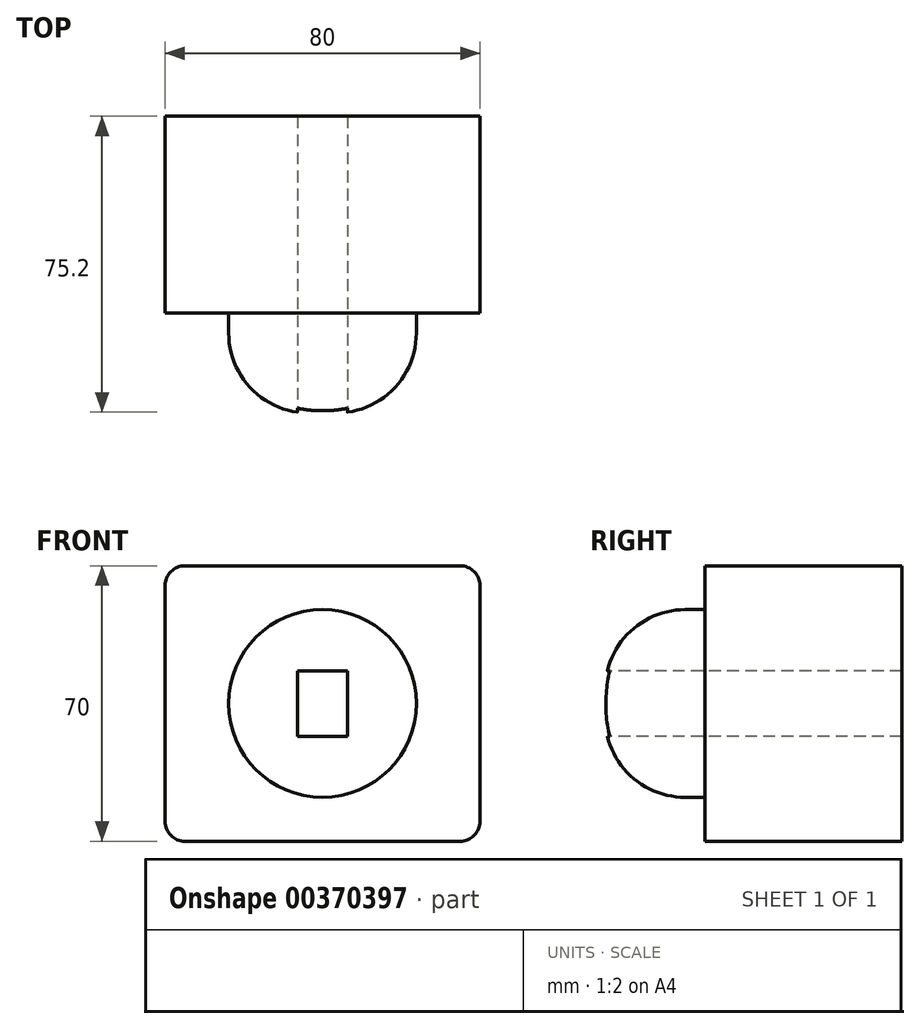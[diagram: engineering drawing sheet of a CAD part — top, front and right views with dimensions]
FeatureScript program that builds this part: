
annotation { "Feature Type Name" : "Feature", "Feature Type Description" : "" }
export const myFeature = defineFeature(function(context is Context, id is Id, definition is map)
    precondition{}
    {
        {
            var Q0;
            Q0=qCreatedBy(makeId("Front.planeOp"),FACE);
            var sketch = newSketch(context, id + "F0", { "sketchPlane" : qUnion([Q0])});
            skLineSegment(sketch, "E0.bottom", {"start": v(40, -35) * mm, "end": v(-40, -35) * mm});
            skLineSegment(sketch, "E0.top", {"start": v(40, 35) * mm, "end": v(-40, 35) * mm});
            skLineSegment(sketch, "E0.left", {"start": v(40, -35) * mm, "end": v(40, 35) * mm});
            skLineSegment(sketch, "E0.right", {"start": v(-40, -35) * mm, "end": v(-40, 35) * mm});
            skPoint(sketch, "E0.middle", {"position": v(0, 0) * mm});
            skSolve(sketch);
        }
        {
            var Q0;
            Q0=makeQuery(id+"F0.imprint","IMPRINT",FACE,{"disambiguationData":[TD([[makeQuery(id+"F0.imprint","IMPRINT",EDGE,{"derivedFrom":sQuery(id+"F0.wireOp",EDGE,"E0.bottom")}),-1.0]])]});
            extrude(context, id + "F1", {"entities" : qUnion([Q0]), "depth" : 50 * mm});
        }
        {
            var Q0;
            Q0=makeQuery(id+"F1.opExtrude","CAP_FACE",FACE,{"disambiguationData":[OSD([sQuery(id+"F0.wireOp",EDGE,"E0.bottom"),sQuery(id+"F0.wireOp",EDGE,"E0.top"),sQuery(id+"F0.wireOp",EDGE,"E0.left"),sQuery(id+"F0.wireOp",EDGE,"E0.right")])],"isStart":false});
            var sketch = newSketch(context, id + "F2", { "sketchPlane" : qUnion([Q0])});
            skCircle(sketch, "E1", {"center": v(0, 0) * mm, "radius": 23.84 * mm});
            skSolve(sketch);
        }
        {
            var Q0;
            Q0=makeQuery(id+"F2.imprint","IMPRINT",FACE,{"disambiguationData":[TD([[makeQuery(id+"F2.imprint","IMPRINT",EDGE,{"derivedFrom":sQuery(id+"F2.wireOp",EDGE,"E1")}),1.0]])]});
            extrude(context, id + "F3", {"entities" : qUnion([Q0]), "operationType" : NewBodyOperationType.ADD, "depth" : 25.4 * mm});
        }
        {
            var Q0;
            Q0=makeQuery(id+"F1.opExtrude","SWEPT_EDGE",EDGE,{"disambiguationData":[OSD([sQuery(id+"F0.wireOp",EDGE,"E0.top"),sQuery(id+"F0.wireOp",EDGE,"E0.left")])]});
            var Q1;
            Q1=makeQuery(id+"F1.opExtrude","SWEPT_EDGE",EDGE,{"disambiguationData":[OSD([sQuery(id+"F0.wireOp",EDGE,"E0.bottom"),sQuery(id+"F0.wireOp",EDGE,"E0.left")])]});
            var Q2;
            Q2=makeQuery(id+"F1.opExtrude","SWEPT_EDGE",EDGE,{"disambiguationData":[OSD([sQuery(id+"F0.wireOp",EDGE,"E0.top"),sQuery(id+"F0.wireOp",EDGE,"E0.right")])]});
            var Q3;
            Q3=makeQuery(id+"F1.opExtrude","SWEPT_EDGE",EDGE,{"disambiguationData":[OSD([sQuery(id+"F0.wireOp",EDGE,"E0.bottom"),sQuery(id+"F0.wireOp",EDGE,"E0.right")])]});
            fillet(context, id + "F4", {"entities" : qUnion([Q0, Q1, Q2, Q3]), "radius" : 5.08 * mm, "tangentPropagation" : true, "allowEdgeOverflow" : false});
        }
        {
            var Q0;
            Q0=makeQuery(id+"F3.opExtrude","CAP_EDGE",EDGE,{"disambiguationData":[OSD([sQuery(id+"F2.wireOp",EDGE,"E1")])],"isStart":false});
            fillet(context, id + "F5", {"entities" : qUnion([Q0]), "radius" : 20.32 * mm, "tangentPropagation" : true, "allowEdgeOverflow" : false});
        }
        {
            var Q0;
            Q0=makeQuery(id+"F3.opExtrude","CAP_FACE",FACE,{"disambiguationData":[OSD([sQuery(id+"F2.wireOp",EDGE,"E1")])],"isStart":false});
            var sketch = newSketch(context, id + "F6", { "sketchPlane" : qUnion([Q0])});
            skLineSegment(sketch, "E2.bottom", {"start": v(6.35, 8.33) * mm, "end": v(-6.35, 8.33) * mm});
            skLineSegment(sketch, "E2.top", {"start": v(6.35, -8.33) * mm, "end": v(-6.35, -8.33) * mm});
            skLineSegment(sketch, "E2.left", {"start": v(6.35, 8.33) * mm, "end": v(6.35, -8.33) * mm});
            skLineSegment(sketch, "E2.right", {"start": v(-6.35, 8.33) * mm, "end": v(-6.35, -8.33) * mm});
            skPoint(sketch, "E2.middle", {"position": v(0, 0) * mm});
            skSolve(sketch);
        }
        {
            var Q0;
            Q0 = qSketchRegion(id + "F6", true);
            extrude(context, id + "F7", {"entities" : qUnion([Q0]), "operationType" : NewBodyOperationType.REMOVE, "endBound" : BoundingType.UP_TO_NEXT, "oppositeDirection" : true, "depth" : 25.4 * mm});
        }
    });
